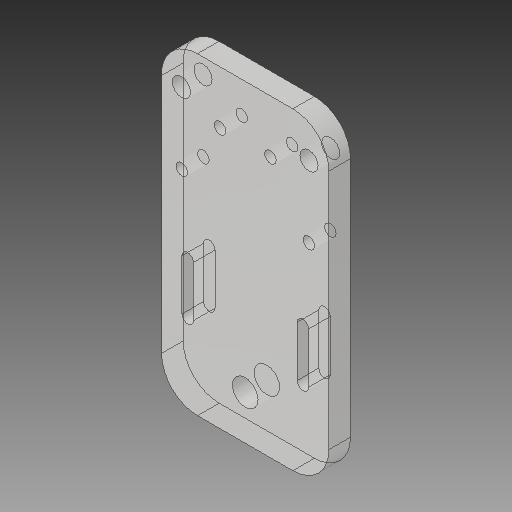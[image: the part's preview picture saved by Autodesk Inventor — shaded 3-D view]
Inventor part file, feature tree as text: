
AUTODESK INVENTOR PART (.ipt)
format: ipt  version: 2017 (Build 210142000, 142)  size: 185,344 bytes
history: native  units: mm
features: other x3, sketch x2
ambient origin geometry x8: Origin, YZ Plane, XZ Plane, XY Plane, X Axis, Y Axis, Z Axis, Center Point
bodies: Solid1 (feature_tree)
feature tree (5):
  other  "Hotend Front Plate revised.ipt"
  other  "Solid1::Hotend Front Plate revised.ipt"
  other  "TaggingFeature1"
  sketch  "Sketch1"  dims[d0=10.0mm]
  sketch  "Sketch2"
